# Revit family: Firestop-SpeedFlex-STI-Joint_Profile
name_source: partatom
category: Specialty Equipment
units: mm (PartAtom-declared; Revit-internal decimal feet)

## family parameters
Classification Number = 23.20.50.14
Cut with Voids When Loaded = No
Enable Cutting in Views = No
Maintain Annotation Orientation = No
Part Type = Normal
Room Calculation Point = No
Round Connector Dimension = Use Diameter
Shared = No

## types (1)
- SFJP40
    Assembly Code = D4030900
    Default Elevation = 0' - 0"
    Description = replaces strips of mineral wool
    Fiber = Firestopping-STI-Speed-Flex-Joint-Profile
    General Information = http://files.systems.stifirestop.com
    Green Building/LEED® Information = http://sti.fmpdata.net
    Guide Specification = http://www.stifirestop.com
    Locate Distributor = http://www.stifirestop.com
    MSDS = http://files.systems.stifirestop.com
    Manufacturer = Specified Technologies Inc.
    Manufacturer Fax No. = 908.526.9623
    Model = SFJP40
    Product Data = http://www.stifirestop.com
    Tested Systems = http://sti.fmpdata.net
    URL = http://www.stifirestop.com

## geometry (parser evidence)
native form markers: Blend x1, Sweep x2
no freeform markers — native parametric forms only
